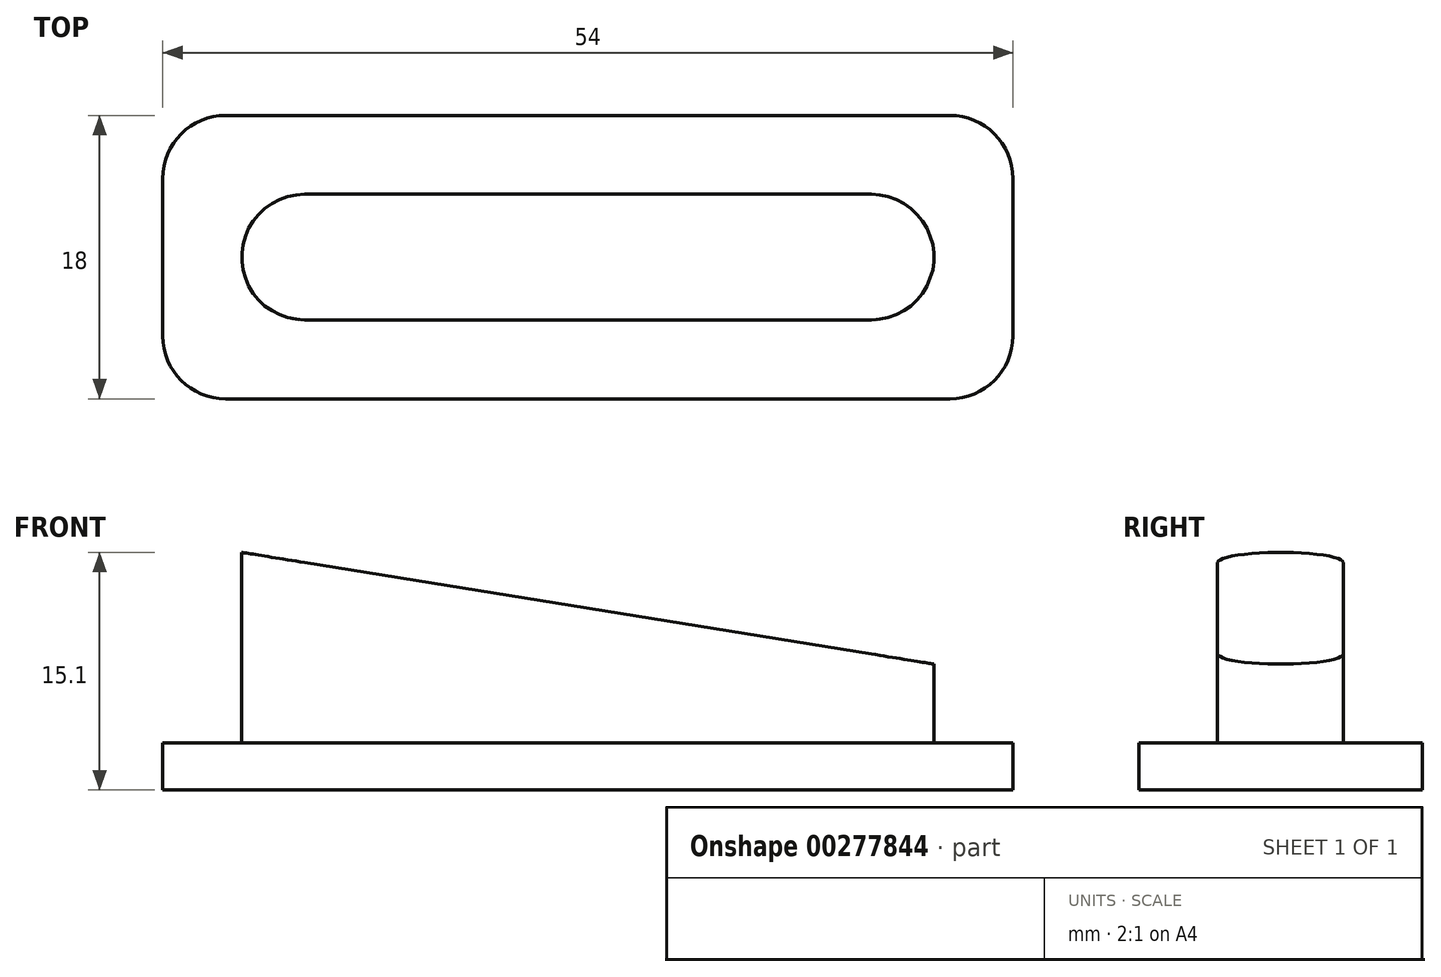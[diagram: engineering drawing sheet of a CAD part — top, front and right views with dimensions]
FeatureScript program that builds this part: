
annotation { "Feature Type Name" : "Feature", "Feature Type Description" : "" }
export const myFeature = defineFeature(function(context is Context, id is Id, definition is map)
    precondition{}
    {
        {
            var Q0;
            Q0=qCreatedBy(makeId("Front.planeOp"),FACE);
            var sketch = newSketch(context, id + "F0", { "sketchPlane" : qUnion([Q0])});
            skLineSegment(sketch, "E0", {"start": v(5, 0) * mm, "end": v(-49, 0) * mm});
            skLineSegment(sketch, "E1", {"start": v(-49, 0) * mm, "end": v(-49, 3) * mm});
            skLineSegment(sketch, "E2", {"start": v(-49, 3) * mm, "end": v(-44, 3) * mm});
            skLineSegment(sketch, "E3", {"start": v(-44, 3) * mm, "end": v(-44, 15.1) * mm});
            skLineSegment(sketch, "E4", {"start": v(-44, 15.1) * mm, "end": v(0, 8) * mm});
            skLineSegment(sketch, "E5", {"start": v(0, 8) * mm, "end": v(0, 3) * mm});
            skLineSegment(sketch, "E6", {"start": v(0, 3) * mm, "end": v(5, 3) * mm});
            skLineSegment(sketch, "E7", {"start": v(5, 3) * mm, "end": v(5, 0) * mm});
            skPoint(sketch, "E8.orphan", {"position": v(5, 0) * mm});
            skSolve(sketch);
        }
        {
            var Q0;
            Q0=makeQuery(id+"F0.imprint","IMPRINT",FACE,{"disambiguationData":[TD([[makeQuery(id+"F0.imprint","IMPRINT",EDGE,{"derivedFrom":sQuery(id+"F0.wireOp",EDGE,"E0")}),-1.0]])]});
            extrude(context, id + "F1", {"entities" : qUnion([Q0]), "endBound" : BoundingType.SYMMETRIC, "depth" : 8 * mm});
        }
        {
            var Q0;
            Q0=makeQuery(id+"F1.opExtrude","SWEPT_FACE",FACE,{"disambiguationData":[OSD([sQuery(id+"F0.wireOp",EDGE,"E0")])]});
            var sketch = newSketch(context, id + "F2", { "sketchPlane" : qUnion([Q0])});
            skLineSegment(sketch, "E9.0", {"start": v(-49, 9) * mm, "end": v(-49, -9) * mm});
            skLineSegment(sketch, "E10.0", {"start": v(5, 9) * mm, "end": v(5, -9) * mm});
            skLineSegment(sketch, "E11", {"start": v(-49, 9) * mm, "end": v(5, 9) * mm});
            skLineSegment(sketch, "E12", {"start": v(-49, -9) * mm, "end": v(5, -9) * mm});
            skPoint(sketch, "E13.orphan", {"position": v(-49, 4) * mm});
            skPoint(sketch, "E14.orphan", {"position": v(5, 4) * mm});
            skPoint(sketch, "E15.orphan", {"position": v(5, -4) * mm});
            skPoint(sketch, "E16.orphan", {"position": v(-49, -4) * mm});
            skSolve(sketch);
        }
        {
            var Q0;
            Q0 = qSketchRegion(id + "F2", true);
            var Q1;
            Q1=makeQuery(id+"F1.opExtrude","SWEPT_FACE",FACE,{"disambiguationData":[OSD([sQuery(id+"F0.wireOp",EDGE,"E6")])]});
            extrude(context, id + "F3", {"entities" : qUnion([Q0]), "operationType" : NewBodyOperationType.ADD, "endBound" : BoundingType.UP_TO_SURFACE, "oppositeDirection" : true, "endBoundEntityFace" : qUnion([Q1]), "depth" : 25 * mm});
        }
        {
            var Q0;
            Q0=makeQuery(id+"F1.opExtrude","CAP_EDGE",EDGE,{"disambiguationData":[OSD([sQuery(id+"F0.wireOp",EDGE,"E5")])],"isStart":false});
            var Q1;
            Q1=makeQuery(id+"F1.opExtrude","CAP_EDGE",EDGE,{"disambiguationData":[OSD([sQuery(id+"F0.wireOp",EDGE,"E5")])],"isStart":true});
            var Q2;
            Q2=makeQuery(id+"F1.opExtrude","CAP_EDGE",EDGE,{"disambiguationData":[OSD([sQuery(id+"F0.wireOp",EDGE,"E3")])],"isStart":true});
            var Q3;
            Q3=makeQuery(id+"F1.opExtrude","CAP_EDGE",EDGE,{"disambiguationData":[OSD([sQuery(id+"F0.wireOp",EDGE,"E3")])],"isStart":false});
            var Q4;
            Q4=makeQuery(id+"F3.opExtrude","SWEPT_EDGE",EDGE,{"disambiguationData":[OSD([sQuery(id+"F2.wireOp",EDGE,"E9.0"),sQuery(id+"F2.wireOp",EDGE,"E11")])]});
            var Q5;
            Q5=makeQuery(id+"F3.opExtrude","SWEPT_EDGE",EDGE,{"disambiguationData":[OSD([sQuery(id+"F2.wireOp",EDGE,"E9.0"),sQuery(id+"F2.wireOp",EDGE,"E12")])]});
            var Q6;
            Q6=makeQuery(id+"F3.opExtrude","SWEPT_EDGE",EDGE,{"disambiguationData":[OSD([sQuery(id+"F2.wireOp",EDGE,"E10.0"),sQuery(id+"F2.wireOp",EDGE,"E12")])]});
            var Q7;
            Q7=makeQuery(id+"F3.opExtrude","SWEPT_EDGE",EDGE,{"disambiguationData":[OSD([sQuery(id+"F2.wireOp",EDGE,"E10.0"),sQuery(id+"F2.wireOp",EDGE,"E11")])]});
            fillet(context, id + "F4", {"entities" : qUnion([Q0, Q1, Q2, Q3, Q4, Q5, Q6, Q7]), "radius" : 4 * mm, "tangentPropagation" : true, "allowEdgeOverflow" : false});
        }
    });
